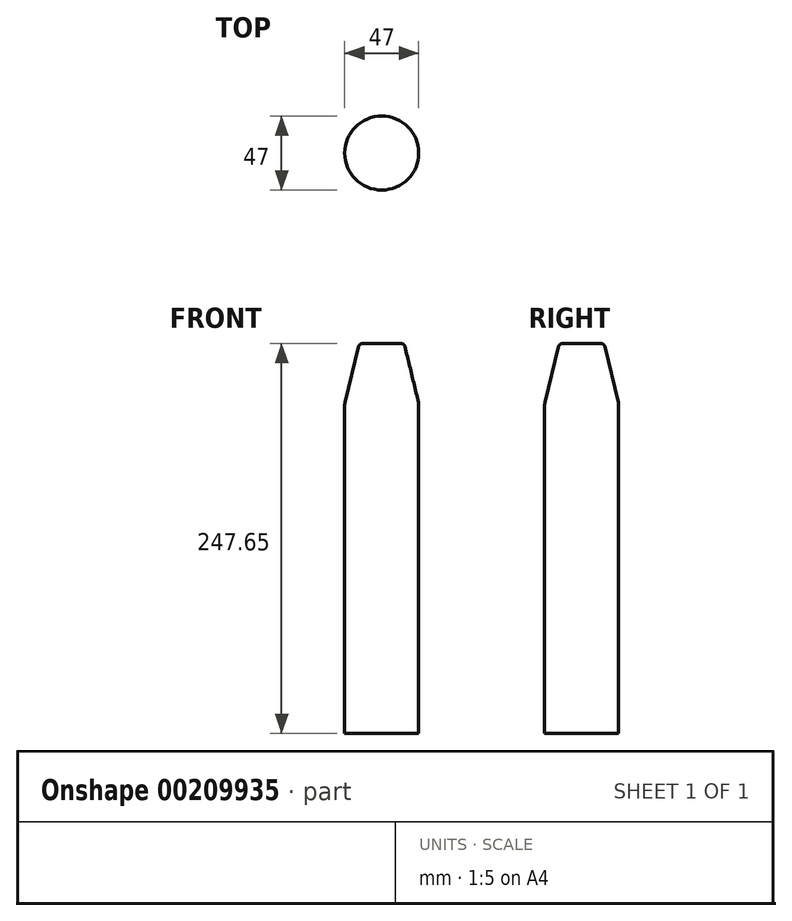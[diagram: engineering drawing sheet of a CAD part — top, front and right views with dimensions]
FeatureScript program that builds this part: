
annotation { "Feature Type Name" : "Feature", "Feature Type Description" : "" }
export const myFeature = defineFeature(function(context is Context, id is Id, definition is map)
    precondition{}
    {
        {
            var Q0;
            Q0=qCreatedBy(makeId("Front.planeOp"),FACE);
            var sketch = newSketch(context, id + "F0", { "sketchPlane" : qUnion([Q0])});
            skLineSegment(sketch, "E0", {"start": v(0, -56.96) * mm, "end": v(0, 67.27) * mm, "construction": true});
            skLineSegment(sketch, "E1", {"start": v(0, 0) * mm, "end": v(23.5, 0) * mm});
            skLineSegment(sketch, "E2", {"start": v(23.5, 0) * mm, "end": v(23.5, 209.55) * mm});
            skLineSegment(sketch, "E3", {"start": v(23.5, 209.55) * mm, "end": v(14.29, 247.65) * mm});
            skLineSegment(sketch, "E4", {"start": v(14.29, 247.65) * mm, "end": v(0, 247.65) * mm});
            skLineSegment(sketch, "E5", {"start": v(0, 247.65) * mm, "end": v(0, 0) * mm});
            skSolve(sketch);
        }
        {
            var Q0;
            Q0 = qSketchRegion(id + "F0", true);
            var Q1;
            Q1=sQuery(id+"F0.wireOp",EDGE,"E0");
            revolve(context, id + "F1", {"entities" : qUnion([Q0]), "axis" : qUnion([Q1]), "revolveType" : RevolveType.FULL});
        }
        {
            var Q0;
            Q0=makeQuery(id+"F1.opRevolve","SWEPT_EDGE",EDGE,{"disambiguationData":[OSD([sQuery(id+"F0.wireOp",EDGE,"E3"),sQuery(id+"F0.wireOp",EDGE,"E4")])]});
            fillet(context, id + "F2", {"entities" : qUnion([Q0]), "radius" : 2.54 * mm, "tangentPropagation" : true, "allowEdgeOverflow" : false});
        }
        {
            var Q0;
            Q0=makeQuery(id+"F1.opRevolve","SWEPT_EDGE",EDGE,{"disambiguationData":[OSD([sQuery(id+"F0.wireOp",EDGE,"E2"),sQuery(id+"F0.wireOp",EDGE,"E3")])]});
            fillet(context, id + "F3", {"entities" : qUnion([Q0]), "radius" : 5.08 * mm, "tangentPropagation" : true, "allowEdgeOverflow" : false});
        }
    });
